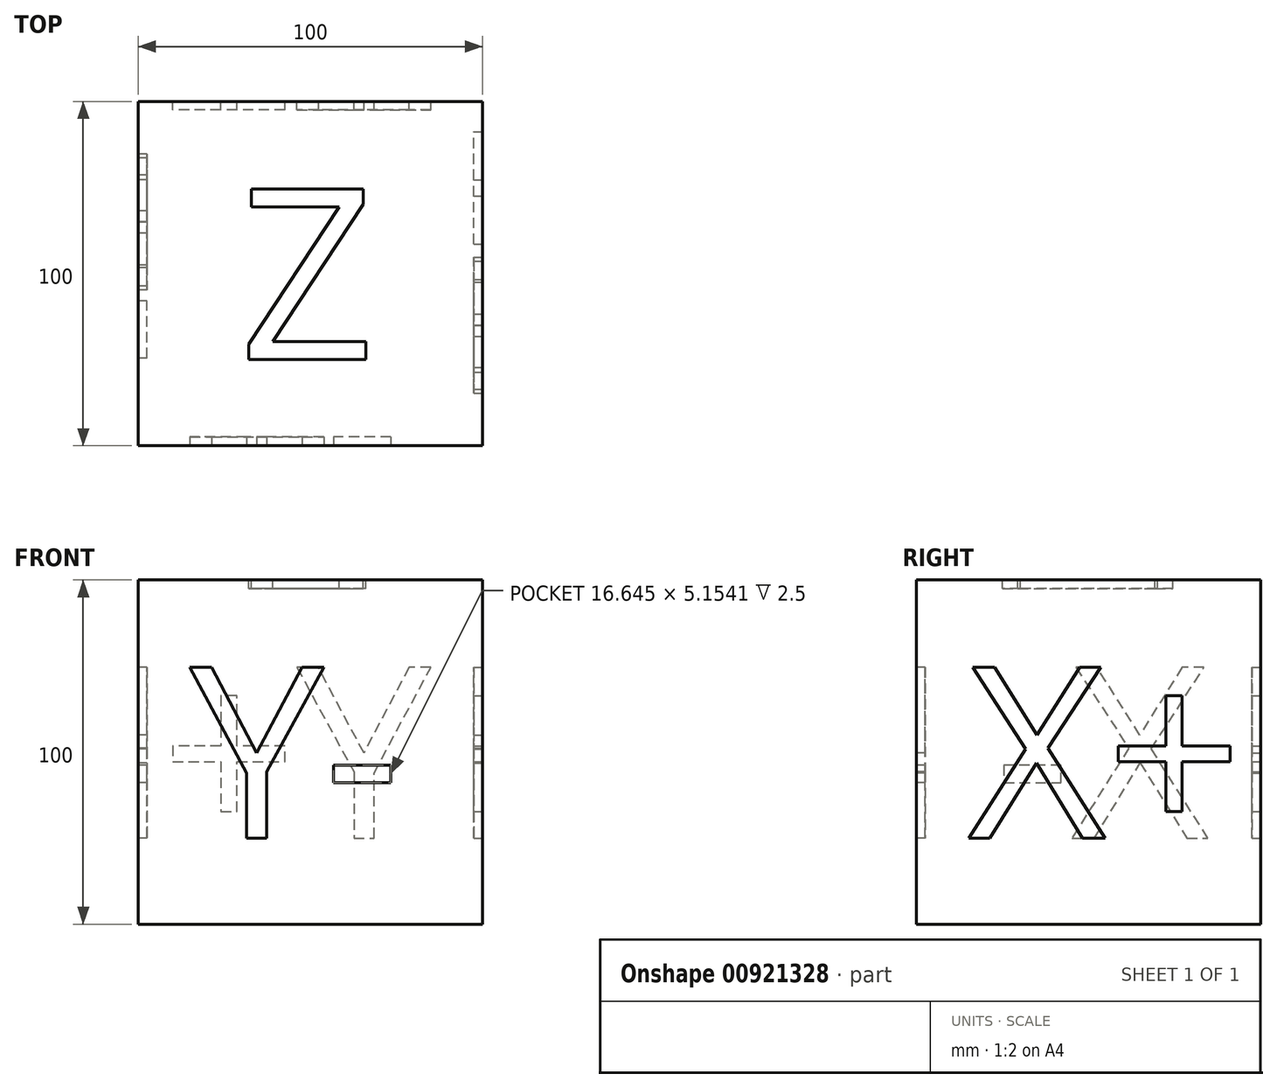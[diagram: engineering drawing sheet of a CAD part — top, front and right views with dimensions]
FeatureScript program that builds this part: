
annotation { "Feature Type Name" : "Feature", "Feature Type Description" : "" }
export const myFeature = defineFeature(function(context is Context, id is Id, definition is map)
    precondition{}
    {
        {
            var Q0;
            Q0=qCreatedBy(makeId("Top.planeOp"),FACE);
            var sketch = newSketch(context, id + "F0", { "sketchPlane" : qUnion([Q0])});
            skLineSegment(sketch, "E0.bottom", {"start": v(0, 0) * mm, "end": v(100, 0) * mm});
            skLineSegment(sketch, "E0.top", {"start": v(0, 100) * mm, "end": v(100, 100) * mm});
            skLineSegment(sketch, "E0.left", {"start": v(0, 0) * mm, "end": v(0, 100) * mm});
            skLineSegment(sketch, "E0.right", {"start": v(100, 0) * mm, "end": v(100, 100) * mm});
            skSolve(sketch);
        }
        {
            var Q0;
            Q0=makeQuery(id+"F0.imprint","IMPRINT",FACE,{"disambiguationData":[TD([[makeQuery(id+"F0.imprint","IMPRINT",EDGE,{"derivedFrom":sQuery(id+"F0.wireOp",EDGE,"E0.bottom")}),1.0]])]});
            extrude(context, id + "F1", {"entities" : qUnion([Q0]), "depth" : 100 * mm, "offsetDistance" : 25 * mm});
        }
        {
            var Q0;
            Q0=makeQuery(id+"F1.opExtrude","SWEPT_FACE",FACE,{"disambiguationData":[OSD([sQuery(id+"F0.wireOp",EDGE,"E0.right")])]});
            var sketch = newSketch(context, id + "F2", { "sketchPlane" : qUnion([Q0])});
            skText(sketch, "E1", { "text": "X+", "fontName": "OpenSans-Regular.ttf"});
            const initialGuessF2  = {"E1": [0.015, 0.025, 1, 0, 0.05]};
            skSetInitialGuess(sketch, initialGuessF2);
            skSolve(sketch);
        }
        {
            var Q0;
            Q0 = qSketchRegion(id + "F2", true);
            extrude(context, id + "F3", {"entities" : qUnion([Q0]), "operationType" : NewBodyOperationType.REMOVE, "oppositeDirection" : true, "depth" : 2.5 * mm, "offsetDistance" : 25 * mm});
        }
        {
            var Q0;
            Q0=makeQuery(id+"F1.opExtrude","SWEPT_FACE",FACE,{"disambiguationData":[OSD([sQuery(id+"F0.wireOp",EDGE,"E0.left")])]});
            var sketch = newSketch(context, id + "F4", { "sketchPlane" : qUnion([Q0])});
            skText(sketch, "E2", { "text": "X-", "fontName": "OpenSans-Regular.ttf"});
            const initialGuessF4  = {"E2": [-0.085, 0.025, 1, 0, 0.05]};
            skSetInitialGuess(sketch, initialGuessF4);
            skSolve(sketch);
        }
        {
            var Q0;
            Q0 = qSketchRegion(id + "F4", true);
            extrude(context, id + "F5", {"entities" : qUnion([Q0]), "operationType" : NewBodyOperationType.REMOVE, "oppositeDirection" : true, "depth" : 2.5 * mm, "offsetDistance" : 25 * mm});
        }
        {
            var Q0;
            Q0=makeQuery(id+"F1.opExtrude","SWEPT_FACE",FACE,{"disambiguationData":[OSD([sQuery(id+"F0.wireOp",EDGE,"E0.bottom")])]});
            var sketch = newSketch(context, id + "F6", { "sketchPlane" : qUnion([Q0])});
            skText(sketch, "E3", { "text": "Y-", "fontName": "OpenSans-Regular.ttf"});
            const initialGuessF6  = {"E3": [0.015, 0.025, 1, 0, 0.05]};
            skSetInitialGuess(sketch, initialGuessF6);
            skSolve(sketch);
        }
        {
            var Q0;
            Q0 = qSketchRegion(id + "F6", true);
            extrude(context, id + "F7", {"entities" : qUnion([Q0]), "operationType" : NewBodyOperationType.REMOVE, "oppositeDirection" : true, "depth" : 2.5 * mm, "offsetDistance" : 25 * mm});
        }
        {
            var Q0;
            Q0=makeQuery(id+"F1.opExtrude","SWEPT_FACE",FACE,{"disambiguationData":[OSD([sQuery(id+"F0.wireOp",EDGE,"E0.top")])]});
            var sketch = newSketch(context, id + "F8", { "sketchPlane" : qUnion([Q0])});
            skText(sketch, "E4", { "text": "Y+", "fontName": "OpenSans-Regular.ttf"});
            const initialGuessF8  = {"E4": [-0.085, 0.025, 1, 0, 0.05]};
            skSetInitialGuess(sketch, initialGuessF8);
            skSolve(sketch);
        }
        {
            var Q0;
            Q0 = qSketchRegion(id + "F8", true);
            extrude(context, id + "F9", {"entities" : qUnion([Q0]), "operationType" : NewBodyOperationType.REMOVE, "oppositeDirection" : true, "depth" : 2.5 * mm, "offsetDistance" : 25 * mm});
        }
        {
            var Q0;
            Q0=makeQuery(id+"F1.opExtrude","CAP_FACE",FACE,{"disambiguationData":[OSD([sQuery(id+"F0.wireOp",EDGE,"E0.bottom"),sQuery(id+"F0.wireOp",EDGE,"E0.top"),sQuery(id+"F0.wireOp",EDGE,"E0.left"),sQuery(id+"F0.wireOp",EDGE,"E0.right")])],"isStart":false});
            var sketch = newSketch(context, id + "F10", { "sketchPlane" : qUnion([Q0])});
            skText(sketch, "E5", { "text": "Z", "fontName": "OpenSans-Regular.ttf"});
            const initialGuessF10  = {"E5": [0.02932, 0.025, 1, 0, 0.05]};
            skSetInitialGuess(sketch, initialGuessF10);
            skSolve(sketch);
        }
        {
            var Q0;
            Q0 = qSketchRegion(id + "F10", true);
            extrude(context, id + "F11", {"entities" : qUnion([Q0]), "operationType" : NewBodyOperationType.REMOVE, "oppositeDirection" : true, "depth" : 2.5 * mm, "offsetDistance" : 25 * mm});
        }
    });
